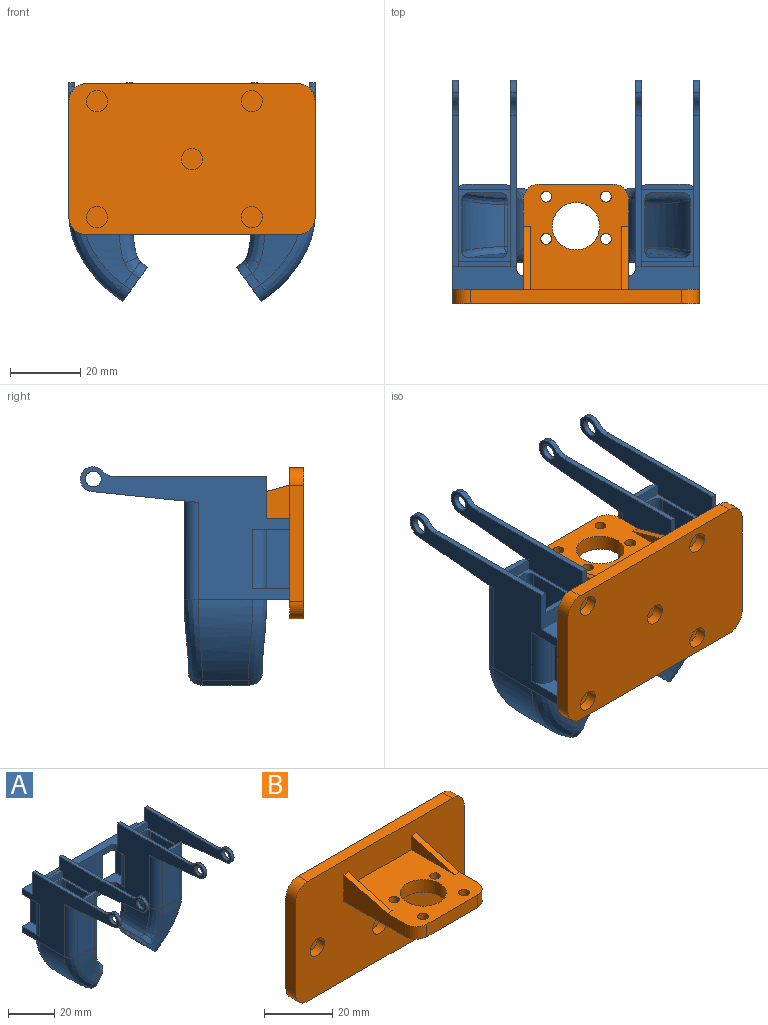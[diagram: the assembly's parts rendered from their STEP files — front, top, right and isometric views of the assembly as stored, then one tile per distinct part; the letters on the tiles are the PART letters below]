
ASSEMBLY  parts=2 mates=1
PART A: 184 faces, bbox 75x64.5x67.1 mm
  f0: bspline ~4.72x4.44mm, area 14.5mm2, adj f59,f61,f87,f88
  f1: bspline ~4.72x4.44mm, area 14.5mm2, adj f57,f59,f84,f85
  f2: plane 12x10.5mm, normal (0,0,-1), area 64.8mm2, adj f7,f21,f32,f33,f75,f76,f78,f89
  f3: plane 17x1mm, normal (0,1,0), area 17mm2, adj f5,f22,f77,f90
  f4: plane 12x10.5mm, normal (0,0,1), area 64.8mm2, adj f7,f21,f32,f33,f35,f75,f78,f89
  f5: plane 10.5x5mm, normal (0,0,-1), area 35.9mm2, adj f3,f33,f34,f77,f90
  f6: plane 18x12mm, normal (0,1,0), area 111mm2, adj f11,f18,f20,f21,f34,f46,f53,f74
  f7: plane 17x1mm, normal (0,1,0), area 17mm2, adj f2,f4,f78,f89
  f8: plane 30.39x3.12mm, normal (0,-0.1,-0.99), area 42.5mm2, adj f13,f20,f21,f86
  f9: plane 1.5x0.06mm, normal (0,-1,0), area 0.1mm2, adj f13,f14,f20,f21
  f10: plane 1.5x0.07mm, normal (0,0,1), area 0.1mm2, adj f14,f15,f20,f21
  f11: plane 43.1x1.5mm, normal (0,0,1), area 64.7mm2, adj f6,f16,f20,f21
  f12: cylinder r=2.25mm len=4.5mm, axis (-1,0,0), area 21.2mm2, adj f20,f21
  f13: cylinder r=3.5mm len=3.48mm, axis (1,0,0), area 7.7mm2, adj f8,f9,f20,f21
  f14: cylinder r=3.5mm len=3.5mm, axis (-1,0,0), area 8.2mm2, adj f9,f10,f20,f21
  f15: cylinder r=3.5mm len=2.6mm, axis (1,0,0), area 4.4mm2, adj f10,f16,f20,f21
  f16: cylinder r=5mm len=3.73mm, axis (1,0,0), area 6.3mm2, adj f11,f15,f20,f21
  f17: plane 15x3mm, normal (0,-1,0), area 45mm2, adj f18,f20,f42,f53
  f18: plane 53x12.73mm, normal (1,0,0), area 383.2mm2, adj f6,f17,f19,f42,f43,f44,f45,f46
  f19: plane 15x3mm, normal (0,1,0), area 45mm2, adj f18,f20,f42,f52
  f20: plane 53x12.73mm, normal (-1,0,0), area 383.2mm2, adj f6,f8,f9,f10,f11,f12,f13,f14
  f21: plane 53.5x37.73mm, normal (1,0,0), area 803.5mm2, adj f2,f4,f6,f8,f9,f10,f11,f12
  f22: plane 10.5x5mm, normal (0,0,1), area 35.9mm2, adj f3,f33,f34,f77,f90
  f23: plane 3.9x3.79mm, normal (0,-1,0), area 7.5mm2, adj f29,f31,f68,f71
  f24: plane 12x2.02mm, normal (0.59,0,0.81), area 30mm2, adj f28,f31,f62,f71
  f25: plane 3.9x3.79mm, normal (0,1,0), area 7.5mm2, adj f27,f31,f62,f65
  f26: plane 12x2.02mm, normal (-0.59,0,-0.81), area 30mm2, adj f30,f31,f65,f68
  f27: bspline ~22.88x16.34mm, area 124.1mm2, adj f25,f40,f63,f66
  f28: bspline ~20.91x18.5mm, area 330.1mm2, adj f24,f41,f63,f72
  f29: bspline ~22.87x16.34mm, area 124.1mm2, adj f23,f38,f69,f72
  f30: bspline ~18.5x16.75mm, area 215.3mm2, adj f26,f39,f66,f69
  f31: plane 21x9.71mm, normal (0.81,0,-0.59), area 129.7mm2, adj f23,f24,f25,f26,f55,f56,f58,f60
  f32: plane 30x23mm, normal (0,-1,0), area 520mm2, adj f2,f4,f35,f36,f74,f75,f76,f97
  f33: plane 70x23mm, normal (0,1,0), area 947.2mm2, adj f2,f4,f5,f22,f34,f36,f74,f75
  f34: plane 59.5x37.73mm, normal (-1,0,0), area 839.5mm2, adj f5,f6,f22,f33,f36,f43,f44,f45
  f35: cylinder r=2mm len=3mm, axis (0,0,-1), area 9.4mm2, adj f4,f21,f32,f36
  f36: plane 70.13x10.63mm, normal (0,0,-1), area 385.5mm2, adj f21,f32,f33,f34,f35,f57,f82,f85
  f37: plane 28x10mm, normal (0,-1,0), area 280mm2, adj f52,f61,f79,f86
  f38: plane 25x9mm, normal (0,-1,0), area 225mm2, adj f29,f42,f70,f73
  f39: plane 25x14.5mm, normal (-1,0,0), area 362.5mm2, adj f30,f42,f67,f70
  f40: plane 25x9mm, normal (0,1,0), area 225mm2, adj f27,f42,f64,f67
  f41: plane 25x14.5mm, normal (1,0,0), area 362.5mm2, adj f28,f42,f64,f73
  f42: plane 20.5x15mm, normal (0,0,1), area 70.4mm2, adj f17,f18,f19,f20,f38,f39,f40,f41
  f43: plane 30.39x3.12mm, normal (0,-0.1,-0.99), area 42.5mm2, adj f18,f34,f48,f79
  f44: plane 1.5x0.06mm, normal (0,-1,0), area 0.1mm2, adj f18,f34,f48,f49
  f45: plane 1.5x0.07mm, normal (0,0,1), area 0.1mm2, adj f18,f34,f49,f50
  f46: plane 43.1x1.5mm, normal (0,0,1), area 64.7mm2, adj f6,f18,f34,f51
  f47: cylinder r=2.25mm len=4.5mm, axis (-1,0,0), area 21.2mm2, adj f18,f34
  f48: cylinder r=3.5mm len=3.48mm, axis (1,0,0), area 7.7mm2, adj f18,f34,f43,f44
  f49: cylinder r=3.5mm len=3.5mm, axis (-1,0,0), area 8.2mm2, adj f18,f34,f44,f45
  f50: cylinder r=3.5mm len=2.6mm, axis (1,0,0), area 4.4mm2, adj f18,f34,f45,f51
  f51: cylinder r=5mm len=3.73mm, axis (1,0,0), area 6.3mm2, adj f18,f34,f46,f50
  f52: plane 15x1.5mm, normal (0,0,1), area 21.1mm2, adj f18,f19,f20,f37,f79,f86
  f53: plane 15x1.5mm, normal (0,0,1), area 22.5mm2, adj f6,f17,f18,f20
  f54: offset ~26.41x24.66mm, area 389.1mm2, adj f34,f55,f80,f82
  f55: plane 13x2.02mm, normal (-0.59,0,-0.81), area 32.5mm2, adj f31,f54,f81,f83
  f56: plane 4.71x4.37mm, normal (0,1,0), area 10mm2, adj f31,f57,f83,f84
  f57: offset ~25.26x19.36mm, area 146.7mm2, adj f1,f36,f56,f82,f85
  f58: plane 13x2.02mm, normal (0.59,0,0.81), area 32.5mm2, adj f31,f59,f84,f87
  f59: offset ~24.75x21.79mm, area 199.1mm2, adj f0,f1,f21,f58,f85,f88
  f60: plane 4.71x4.37mm, normal (0,-1,0), area 10mm2, adj f31,f61,f81,f87
  f61: offset ~27.13x22.63mm, area 146.7mm2, adj f0,f37,f60,f80,f88
  f62: cylinder r=2mm len=3.2mm, axis (0.81,0,-0.59), area 7.9mm2, adj f24,f25,f31,f63
  f63: bspline ~22.63x14.14mm, area 75.7mm2, adj f27,f28,f62,f64
  f64: cylinder r=2mm len=25mm, axis (0,0,1), area 78.5mm2, adj f40,f41,f42,f63
  f65: cylinder r=2mm len=3.2mm, axis (-0.81,0,0.59), area 7.9mm2, adj f25,f26,f31,f66
  f66: bspline ~20.32x6.97mm, area 52.6mm2, adj f27,f30,f65,f67
  f67: cylinder r=2mm len=25mm, axis (0,0,1), area 78.5mm2, adj f39,f40,f42,f66
  f68: cylinder r=2mm len=3.2mm, axis (0.81,0,-0.59), area 7.9mm2, adj f23,f26,f31,f69
  f69: bspline ~20.32x6.97mm, area 52.6mm2, adj f29,f30,f68,f70
  f70: cylinder r=2mm len=25mm, axis (0,0,1), area 78.5mm2, adj f38,f39,f42,f69
  f71: cylinder r=2mm len=3.2mm, axis (-0.81,0,0.59), area 7.9mm2, adj f23,f24,f31,f72
  f72: bspline ~22.63x14.14mm, area 75.7mm2, adj f28,f29,f71,f73
  f73: cylinder r=2mm len=25mm, axis (0,0,1), area 78.5mm2, adj f38,f41,f42,f72
  f74: plane 70x6.5mm, normal (0,0,1), area 371.7mm2, adj f6,f21,f32,f33,f34,f76,f101,f116
  f75: plane 17x4mm, normal (-1,0,0), area 68mm2, adj f2,f4,f32,f33
  f76: cylinder r=2mm len=3mm, axis (0,0,-1), area 9.4mm2, adj f2,f21,f32,f74
  f77: plane 17x6.5mm, normal (-1,0,0), area 110.5mm2, adj f3,f5,f22,f33
  f78: plane 17x6.5mm, normal (1,0,0), area 110.5mm2, adj f2,f4,f7,f33
  f79: cylinder r=4mm len=28mm, axis (0,0,1), area 175.1mm2, adj f18,f34,f37,f43,f52,f80
  f80: bspline ~24.38x16.63mm, area 162.1mm2, adj f54,f61,f79,f81
  f81: cylinder r=4mm len=4.71mm, axis (-0.81,0,0.59), area 15.7mm2, adj f31,f55,f60,f80
  f82: bspline ~24.38x16.63mm, area 162.1mm2, adj f36,f54,f57,f83
  f83: cylinder r=4mm len=4.71mm, axis (0.81,0,-0.59), area 15.7mm2, adj f31,f55,f56,f82
  f84: cylinder r=4mm len=4.71mm, axis (-0.81,0,0.59), area 15.7mm2, adj f1,f31,f56,f58
  f85: bspline ~14.88x5.76mm, area 80.2mm2, adj f1,f36,f57,f59
  f86: cylinder r=4mm len=28mm, axis (0,0,1), area 175.1mm2, adj f8,f20,f21,f37,f52,f88
  f87: cylinder r=4mm len=4.71mm, axis (0.81,0,-0.59), area 15.7mm2, adj f0,f31,f58,f60
  f88: bspline ~14.88x5.76mm, area 80.2mm2, adj f0,f59,f61,f86
  f89: cylinder r=4mm len=17mm, axis (0,0,-1), area 106.8mm2, adj f2,f4,f7,f21
  f90: cylinder r=4mm len=17mm, axis (0,0,-1), area 106.8mm2, adj f3,f5,f22,f34
  f91: cylinder r=3mm len=6mm, axis (0,1,0), area 56.5mm2, adj f33,f92
  f92: plane 6x6mm, normal (0,1,0), area 28.3mm2, adj f91
  f93: cylinder r=3mm len=6mm, axis (0,1,0), area 56.5mm2, adj f33,f94
  f94: plane 6x6mm, normal (0,1,0), area 28.3mm2, adj f93
  f95: bspline ~4.72x4.44mm, area 14.5mm2, adj f151,f153,f178,f179
  f96: bspline ~4.72x4.44mm, area 14.5mm2, adj f149,f151,f175,f176
  f97: plane 12x10.5mm, normal (0,0,-1), area 64.8mm2, adj f32,f33,f102,f116,f166,f167,f169,f180
  f98: plane 17x1mm, normal (0,1,0), area 17mm2, adj f100,f117,f168,f181
  f99: plane 12x10.5mm, normal (0,0,1), area 64.8mm2, adj f32,f33,f102,f116,f128,f166,f169,f180
  f100: plane 10.5x5mm, normal (0,0,-1), area 35.9mm2, adj f33,f98,f127,f168,f181
  f101: plane 18x12mm, normal (0,1,0), area 111mm2, adj f74,f106,f113,f115,f116,f127,f138,f145
  f102: plane 17x1mm, normal (0,1,0), area 17mm2, adj f97,f99,f169,f180
  f103: plane 30.39x3.12mm, normal (0,-0.1,-0.99), area 42.5mm2, adj f108,f115,f116,f177
  f104: plane 1.5x0.06mm, normal (0,-1,0), area 0.1mm2, adj f108,f109,f115,f116
  f105: plane 1.5x0.07mm, normal (0,0,1), area 0.1mm2, adj f109,f110,f115,f116
  f106: plane 43.1x1.5mm, normal (0,0,1), area 64.7mm2, adj f101,f111,f115,f116
  f107: cylinder r=2.25mm len=4.5mm, axis (1,0,0), area 21.2mm2, adj f115,f116
  f108: cylinder r=3.5mm len=3.48mm, axis (-1,0,0), area 7.7mm2, adj f103,f104,f115,f116
  f109: cylinder r=3.5mm len=3.5mm, axis (1,0,0), area 8.2mm2, adj f104,f105,f115,f116
  f110: cylinder r=3.5mm len=2.6mm, axis (-1,0,0), area 4.4mm2, adj f105,f111,f115,f116
  f111: cylinder r=5mm len=3.73mm, axis (-1,0,0), area 6.3mm2, adj f106,f110,f115,f116
  f112: plane 15x3mm, normal (0,-1,0), area 45mm2, adj f113,f115,f134,f145
  f113: plane 53x12.73mm, normal (-1,0,0), area 383.2mm2, adj f101,f112,f114,f134,f135,f136,f137,f138
  f114: plane 15x3mm, normal (0,1,0), area 45mm2, adj f113,f115,f134,f144
  f115: plane 53x12.73mm, normal (1,0,0), area 383.2mm2, adj f101,f103,f104,f105,f106,f107,f108,f109
  f116: plane 53.5x37.73mm, normal (-1,0,0), area 803.5mm2, adj f36,f74,f97,f99,f101,f103,f104,f105
  f117: plane 10.5x5mm, normal (0,0,1), area 35.9mm2, adj f33,f98,f127,f168,f181
  f118: plane 3.9x3.79mm, normal (0,-1,0), area 7.5mm2, adj f124,f126,f160,f163
  f119: plane 12x2.02mm, normal (-0.59,0,0.81), area 30mm2, adj f123,f126,f154,f163
  f120: plane 3.9x3.79mm, normal (0,1,0), area 7.5mm2, adj f122,f126,f154,f157
  f121: plane 12x2.02mm, normal (0.59,0,-0.81), area 30mm2, adj f125,f126,f157,f160
  f122: bspline ~22.88x16.34mm, area 124.1mm2, adj f120,f132,f155,f158
  f123: bspline ~20.91x18.5mm, area 330.1mm2, adj f119,f133,f155,f164
  f124: bspline ~22.87x16.34mm, area 124.1mm2, adj f118,f130,f161,f164
  f125: bspline ~18.5x16.75mm, area 215.3mm2, adj f121,f131,f158,f161
  f126: plane 21x9.71mm, normal (-0.81,0,-0.59), area 129.7mm2, adj f118,f119,f120,f121,f147,f148,f150,f152
  f127: plane 59.5x37.73mm, normal (1,0,0), area 839.5mm2, adj f33,f36,f74,f100,f101,f117,f135,f136
  f128: cylinder r=2mm len=3mm, axis (0,0,-1), area 9.4mm2, adj f32,f36,f99,f116
  f129: plane 28x10mm, normal (0,-1,0), area 280mm2, adj f144,f153,f170,f177
  f130: plane 25x9mm, normal (0,-1,0), area 225mm2, adj f124,f134,f162,f165
  f131: plane 25x14.5mm, normal (1,0,0), area 362.5mm2, adj f125,f134,f159,f162
  f132: plane 25x9mm, normal (0,1,0), area 225mm2, adj f122,f134,f156,f159
  f133: plane 25x14.5mm, normal (-1,0,0), area 362.5mm2, adj f123,f134,f156,f165
  f134: plane 20.5x15mm, normal (0,0,1), area 70.4mm2, adj f112,f113,f114,f115,f130,f131,f132,f133
  f135: plane 30.39x3.12mm, normal (0,-0.1,-0.99), area 42.5mm2, adj f113,f127,f140,f170
  f136: plane 1.5x0.06mm, normal (0,-1,0), area 0.1mm2, adj f113,f127,f140,f141
  f137: plane 1.5x0.07mm, normal (0,0,1), area 0.1mm2, adj f113,f127,f141,f142
  f138: plane 43.1x1.5mm, normal (0,0,1), area 64.7mm2, adj f101,f113,f127,f143
  f139: cylinder r=2.25mm len=4.5mm, axis (1,0,0), area 21.2mm2, adj f113,f127
  f140: cylinder r=3.5mm len=3.48mm, axis (-1,0,0), area 7.7mm2, adj f113,f127,f135,f136
  f141: cylinder r=3.5mm len=3.5mm, axis (1,0,0), area 8.2mm2, adj f113,f127,f136,f137
  f142: cylinder r=3.5mm len=2.6mm, axis (-1,0,0), area 4.4mm2, adj f113,f127,f137,f143
  f143: cylinder r=5mm len=3.73mm, axis (-1,0,0), area 6.3mm2, adj f113,f127,f138,f142
  f144: plane 15x1.5mm, normal (0,0,1), area 21.1mm2, adj f113,f114,f115,f129,f170,f177
  f145: plane 15x1.5mm, normal (0,0,1), area 22.5mm2, adj f101,f112,f113,f115
  f146: offset ~25.91x20.5mm, area 389.1mm2, adj f127,f147,f171,f173
  f147: plane 13x2.02mm, normal (0.59,0,-0.81), area 32.5mm2, adj f126,f146,f172,f174
  f148: plane 4.71x4.37mm, normal (0,1,0), area 10mm2, adj f126,f149,f174,f175
  f149: offset ~25.26x19.36mm, area 146.7mm2, adj f36,f96,f148,f173,f176
  f150: plane 13x2.02mm, normal (-0.59,0,0.81), area 32.5mm2, adj f126,f151,f175,f178
  f151: offset ~24.75x21.79mm, area 199.1mm2, adj f95,f96,f116,f150,f176,f179
  f152: plane 4.71x4.37mm, normal (0,-1,0), area 10mm2, adj f126,f153,f172,f178
  f153: offset ~27.13x22.63mm, area 146.7mm2, adj f95,f129,f152,f171,f179
  f154: cylinder r=2mm len=3.2mm, axis (-0.81,0,-0.59), area 7.9mm2, adj f119,f120,f126,f155
  f155: bspline ~22.63x14.14mm, area 75.7mm2, adj f122,f123,f154,f156
  f156: cylinder r=2mm len=25mm, axis (0,0,1), area 78.5mm2, adj f132,f133,f134,f155
  f157: cylinder r=2mm len=3.2mm, axis (0.81,0,0.59), area 7.9mm2, adj f120,f121,f126,f158
  f158: bspline ~20.32x6.97mm, area 52.6mm2, adj f122,f125,f157,f159
  f159: cylinder r=2mm len=25mm, axis (0,0,1), area 78.5mm2, adj f131,f132,f134,f158
  f160: cylinder r=2mm len=3.2mm, axis (-0.81,0,-0.59), area 7.9mm2, adj f118,f121,f126,f161
  f161: bspline ~20.32x6.97mm, area 52.6mm2, adj f124,f125,f160,f162
  f162: cylinder r=2mm len=25mm, axis (0,0,1), area 78.5mm2, adj f130,f131,f134,f161
  f163: cylinder r=2mm len=3.2mm, axis (0.81,0,0.59), area 7.9mm2, adj f118,f119,f126,f164
  f164: bspline ~22.63x14.14mm, area 75.7mm2, adj f123,f124,f163,f165
  f165: cylinder r=2mm len=25mm, axis (0,0,1), area 78.5mm2, adj f130,f133,f134,f164
  f166: plane 17x4mm, normal (1,0,0), area 68mm2, adj f32,f33,f97,f99
  f167: cylinder r=2mm len=3mm, axis (0,0,-1), area 9.4mm2, adj f32,f74,f97,f116
  f168: plane 17x6.5mm, normal (1,0,0), area 110.5mm2, adj f33,f98,f100,f117
  f169: plane 17x6.5mm, normal (-1,0,0), area 110.5mm2, adj f33,f97,f99,f102
  f170: cylinder r=4mm len=28mm, axis (0,0,1), area 175mm2, adj f113,f127,f129,f135,f144,f171
  f171: bspline ~24.38x16.63mm, area 162.1mm2, adj f146,f153,f170,f172
  f172: cylinder r=4mm len=4.71mm, axis (0.81,0,0.59), area 15.7mm2, adj f126,f147,f152,f171
  f173: bspline ~24.38x16.63mm, area 162.1mm2, adj f36,f146,f149,f174
  f174: cylinder r=4mm len=4.71mm, axis (-0.81,0,-0.59), area 15.7mm2, adj f126,f147,f148,f173
  f175: cylinder r=4mm len=4.71mm, axis (0.81,0,0.59), area 15.7mm2, adj f96,f126,f148,f150
  f176: bspline ~14.88x5.76mm, area 80.2mm2, adj f36,f96,f149,f151
  f177: cylinder r=4mm len=28mm, axis (0,0,1), area 175mm2, adj f103,f115,f116,f129,f144,f179
  f178: cylinder r=4mm len=4.71mm, axis (-0.81,0,-0.59), area 15.7mm2, adj f95,f126,f150,f152
  f179: bspline ~14.88x5.76mm, area 80.2mm2, adj f95,f151,f153,f177
  f180: cylinder r=4mm len=17mm, axis (0,0,-1), area 106.8mm2, adj f97,f99,f102,f116
  f181: cylinder r=4mm len=17mm, axis (0,0,-1), area 106.8mm2, adj f98,f100,f117,f127
  f182: cylinder r=3mm len=6mm, axis (0,1,0), area 56.5mm2, adj f33,f183
  f183: plane 6x6mm, normal (0,1,0), area 28.3mm2, adj f182
PART B: 42 faces, bbox 70x34x43 mm
  f0: plane 70x43mm, normal (0,-1,0), area 2748.7mm2, adj f1,f2,f3,f4,f5,f6,f7,f9
  f1: plane 18x5mm, normal (1,0,0), area 45mm2, adj f0,f2,f24
  f2: plane 30x30mm, normal (0,0,1), area 646mm2, adj f0,f1,f13,f14,f15,f16,f17,f18
  f3: plane 30x30mm, normal (0,0,-1), area 718mm2, adj f0,f13,f14,f15,f16,f17,f18,f19
  f4: plane 60x4mm, normal (0,0,-1), area 240mm2, adj f0,f8,f9,f12
  f5: plane 33x4mm, normal (1,0,0), area 132mm2, adj f0,f8,f9,f10
  f6: plane 60x4mm, normal (0,0,1), area 240mm2, adj f0,f8,f10,f11
  f7: plane 33x4mm, normal (-1,0,0), area 132mm2, adj f0,f8,f11,f12
  f8: plane 70x43mm, normal (0,1,0), area 2847.2mm2, adj f4,f5,f6,f7,f9,f10,f11,f12
  f9: cylinder r=5mm len=5mm, axis (0,-1,0), area 31.4mm2, adj f0,f4,f5,f8
  f10: cylinder r=5mm len=5mm, axis (0,1,0), area 31.4mm2, adj f0,f5,f6,f8
  f11: cylinder r=5mm len=5mm, axis (0,-1,0), area 31.4mm2, adj f0,f6,f7,f8
  f12: cylinder r=5mm len=5mm, axis (0,1,0), area 31.4mm2, adj f0,f4,f7,f8
  f13: plane 25.5x9.5mm, normal (-1,0,0), area 159.7mm2, adj f0,f2,f3,f17,f24
  f14: plane 25.5x9.5mm, normal (1,0,0), area 159.7mm2, adj f0,f2,f3,f16,f25
  f15: plane 21x4.5mm, normal (0,-1,0), area 94.5mm2, adj f2,f3,f16,f17
  f16: cylinder r=4.5mm len=4.5mm, axis (0,0,-1), area 31.8mm2, adj f2,f3,f14,f15
  f17: cylinder r=4.5mm len=4.5mm, axis (0,0,1), area 31.8mm2, adj f2,f3,f13,f15
  f18: cylinder r=6.75mm len=13.5mm, axis (0,0,1), area 190.9mm2, adj f2,f3
  f19: cylinder r=1.55mm len=4.5mm, axis (0,0,1), area 43.8mm2, adj f2,f3
  f20: cylinder r=1.55mm len=4.5mm, axis (0,0,1), area 43.8mm2, adj f2,f3
  f21: cylinder r=1.55mm len=4.5mm, axis (0,0,1), area 43.8mm2, adj f2,f3
  f22: cylinder r=1.55mm len=4.5mm, axis (0,0,1), area 43.8mm2, adj f2,f3
  f23: plane 18x5mm, normal (-1,0,0), area 45mm2, adj f0,f2,f25
  f24: plane 18x5mm, normal (0,-0.27,0.96), area 37.4mm2, adj f0,f1,f2,f13
  f25: plane 18x5mm, normal (0,-0.27,0.96), area 37.4mm2, adj f0,f2,f14,f23
  f26: cylinder r=3mm len=6mm, axis (0,1,0), area 56.5mm2, adj f8,f27
  f27: plane 6x6mm, normal (0,1,0), area 28.3mm2, adj f26
  f28: cylinder r=3mm len=6mm, axis (0,1,0), area 56.5mm2, adj f8,f29
  f29: plane 6x6mm, normal (0,1,0), area 28.3mm2, adj f28
  f30: cylinder r=3mm len=6mm, axis (0,1,0), area 56.5mm2, adj f8,f31
  f31: plane 6x6mm, normal (0,1,0), area 28.3mm2, adj f30
  f32: cylinder r=3mm len=6mm, axis (0,1,0), area 56.5mm2, adj f8,f33
  f33: plane 6x6mm, normal (0,1,0), area 28.3mm2, adj f32
  f34: cylinder r=3mm len=6mm, axis (0,1,0), area 56.5mm2, adj f8,f35
  f35: plane 6x6mm, normal (0,1,0), area 28.3mm2, adj f34
  f36: cylinder r=3mm len=6mm, axis (0,-1,0), area 56.5mm2, adj f0,f37
  f37: plane 6x6mm, normal (0,-1,0), area 28.3mm2, adj f36
  f38: cylinder r=3mm len=6mm, axis (0,-1,0), area 56.5mm2, adj f0,f39
  f39: plane 6x6mm, normal (0,-1,0), area 28.3mm2, adj f38
  f40: cylinder r=3mm len=6mm, axis (0,-1,0), area 56.5mm2, adj f0,f41
  f41: plane 6x6mm, normal (0,-1,0), area 28.3mm2, adj f40
PLACE A rot(axis=(0,0,1),180deg) t=(0,51.5,-19.5)mm
PLACE B rot(axis=(0,0,1),180deg) t=(0,6,-3.5)mm
MATE fastened A.f93 <-> B.f38  axis (0,-1,0) through (0,10,-12.5)mm
